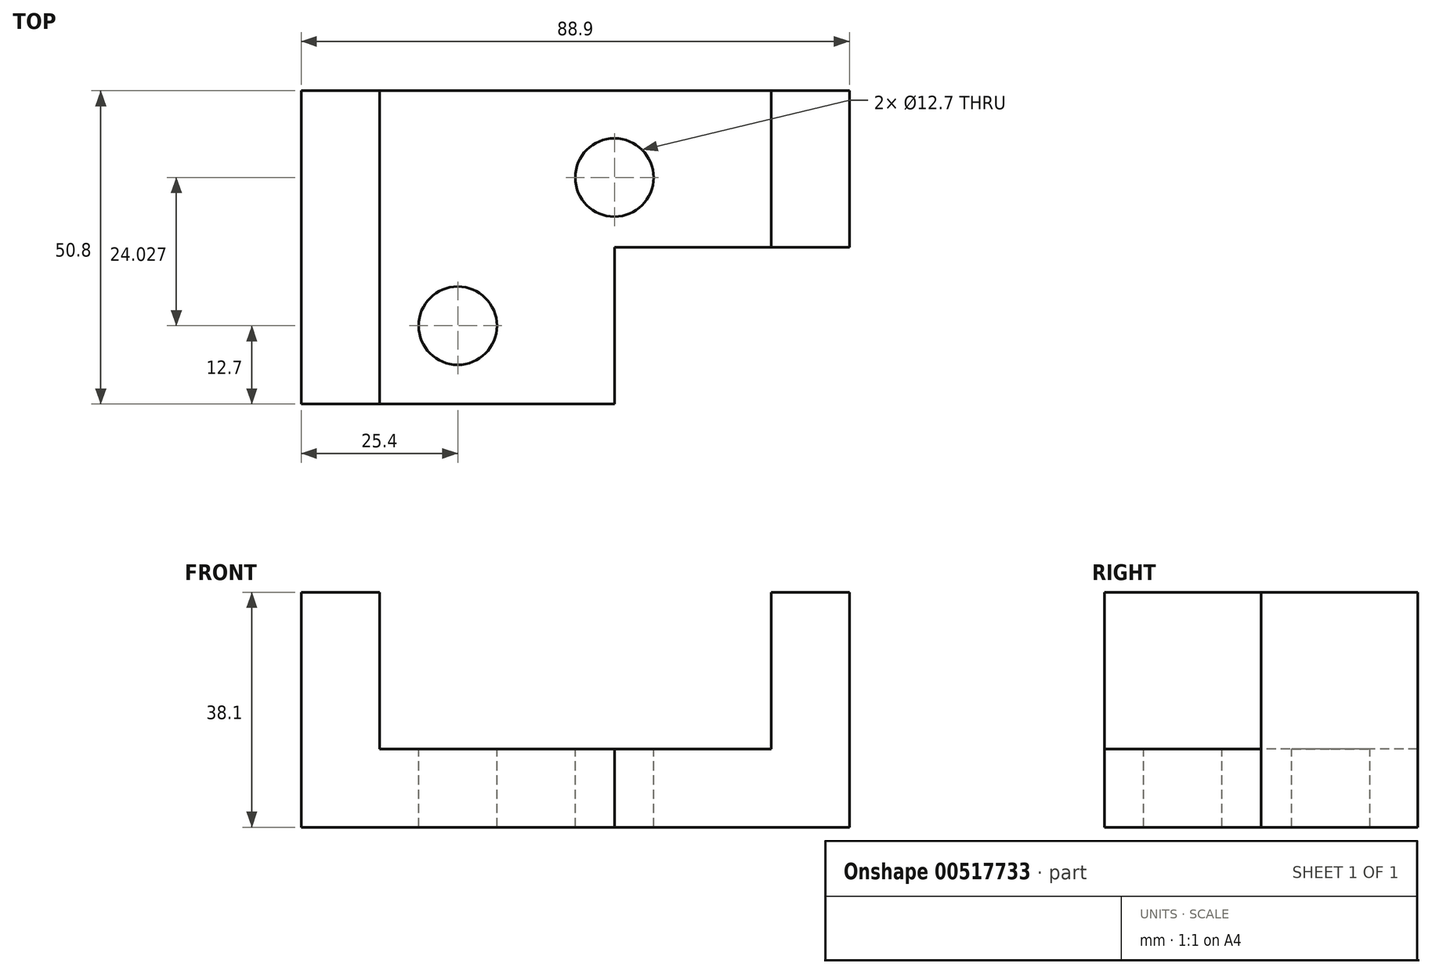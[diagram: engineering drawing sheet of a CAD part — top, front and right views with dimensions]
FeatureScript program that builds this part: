
annotation { "Feature Type Name" : "Feature", "Feature Type Description" : "" }
export const myFeature = defineFeature(function(context is Context, id is Id, definition is map)
    precondition{}
    {
        {
            var Q0;
            Q0=qCreatedBy(makeId("Front.planeOp"),FACE);
            var sketch = newSketch(context, id + "F0", { "sketchPlane" : qUnion([Q0])});
            skLineSegment(sketch, "E0.bottom", {"start": v(-44.45, 19.05) * mm, "end": v(44.45, 19.05) * mm});
            skLineSegment(sketch, "E0.top", {"start": v(-44.45, -19.05) * mm, "end": v(44.45, -19.05) * mm});
            skLineSegment(sketch, "E0.left", {"start": v(-44.45, 19.05) * mm, "end": v(-44.45, -19.05) * mm});
            skLineSegment(sketch, "E0.right", {"start": v(44.45, 19.05) * mm, "end": v(44.45, -19.05) * mm});
            skPoint(sketch, "E0.middle", {"position": v(0, 0) * mm});
            skSolve(sketch);
        }
        {
            var Q0;
            Q0=qSketchRegion(id+"F0",true);
            extrude(context, id + "F1", {"entities" : qUnion([Q0]), "depth" : 50.8 * mm});
        }
        {
            var Q0;
            Q0=makeQuery(id+"F1.opExtrude","CAP_FACE",FACE,{"disambiguationData":[OSD([sQuery(id+"F0.wireOp",EDGE,"E0.bottom"),sQuery(id+"F0.wireOp",EDGE,"E0.top"),sQuery(id+"F0.wireOp",EDGE,"E0.left"),sQuery(id+"F0.wireOp",EDGE,"E0.right")])],"isStart":false});
            var sketch = newSketch(context, id + "F2", { "sketchPlane" : qUnion([Q0])});
            skLineSegment(sketch, "E1.bottom", {"start": v(-31.75, 19.05) * mm, "end": v(31.75, 19.05) * mm});
            skLineSegment(sketch, "E1.top", {"start": v(-31.75, -6.35) * mm, "end": v(31.75, -6.35) * mm});
            skLineSegment(sketch, "E1.left", {"start": v(-31.75, 19.05) * mm, "end": v(-31.75, -6.35) * mm});
            skLineSegment(sketch, "E1.right", {"start": v(31.75, 19.05) * mm, "end": v(31.75, -6.35) * mm});
            skSolve(sketch);
        }
        {
            var Q0;
            Q0=qSketchRegion(id+"F2",true);
            extrude(context, id + "F3", {"entities" : qUnion([Q0]), "operationType" : NewBodyOperationType.REMOVE, "endBound" : BoundingType.THROUGH_ALL, "oppositeDirection" : true, "depth" : 25.4 * mm});
        }
        {
            var Q0;
            {var subQ0=sQuery(id+"F0.wireOp",EDGE,"E0.right");var subQ3=sQuery(id+"F0.wireOp",EDGE,"E0.bottom");Q0=makeQuery(id+"F3.boolean.opBoolean","SPLIT",FACE,{"disambiguationData":[TD([makeQuery(id+"F1.opExtrude","SWEPT_FACE",FACE,{"disambiguationData":[OSD([subQ0])]})])],"derivedFrom":makeQuery(id+"F1.opExtrude","SWEPT_FACE",FACE,{"disambiguationData":[OSD([subQ3])]})});}
            var sketch = newSketch(context, id + "F4", { "sketchPlane" : qUnion([Q0])});
            skLineSegment(sketch, "E2.bottom", {"start": v(44.45, -50.8) * mm, "end": v(6.35, -50.8) * mm});
            skLineSegment(sketch, "E2.top", {"start": v(44.45, -25.4) * mm, "end": v(6.35, -25.4) * mm});
            skLineSegment(sketch, "E2.left", {"start": v(44.45, -50.8) * mm, "end": v(44.45, -25.4) * mm});
            skLineSegment(sketch, "E2.right", {"start": v(6.35, -50.8) * mm, "end": v(6.35, -25.4) * mm});
            skSolve(sketch);
        }
        {
            var Q0;
            Q0=qSketchRegion(id+"F4",true);
            extrude(context, id + "F5", {"entities" : qUnion([Q0]), "operationType" : NewBodyOperationType.REMOVE, "endBound" : BoundingType.THROUGH_ALL, "oppositeDirection" : true, "depth" : 25.4 * mm});
        }
        {
            var Q0;
            Q0=makeQuery(id+"F3.boolean.opBoolean","COPY",FACE,{"derivedFrom":makeQuery(id+"F3.opExtrude","SWEPT_FACE",FACE,{"disambiguationData":[OSD([sQuery(id+"F2.wireOp",EDGE,"E1.top")])]})});
            var sketch = newSketch(context, id + "F6", { "sketchPlane" : qUnion([Q0])});
            skCircle(sketch, "E3", {"center": v(-19.05, -38.1) * mm, "radius": 6.35 * mm});
            skSolve(sketch);
        }
        {
            var Q0;
            Q0=qSketchRegion(id+"F6",true);
            extrude(context, id + "F7", {"entities" : qUnion([Q0]), "operationType" : NewBodyOperationType.REMOVE, "endBound" : BoundingType.THROUGH_ALL, "oppositeDirection" : true, "depth" : 25.4 * mm});
        }
        {
            var Q0;
            Q0=makeQuery(id+"F3.boolean.opBoolean","COPY",FACE,{"derivedFrom":makeQuery(id+"F3.opExtrude","SWEPT_FACE",FACE,{"disambiguationData":[OSD([sQuery(id+"F2.wireOp",EDGE,"E1.top")])]})});
            var sketch = newSketch(context, id + "F8", { "sketchPlane" : qUnion([Q0])});
            skCircle(sketch, "E4", {"center": v(6.35, -14.07) * mm, "radius": 6.35 * mm});
            skSolve(sketch);
        }
        {
            var Q0;
            Q0=qSketchRegion(id+"F8",true);
            extrude(context, id + "F9", {"entities" : qUnion([Q0]), "operationType" : NewBodyOperationType.REMOVE, "endBound" : BoundingType.THROUGH_ALL, "oppositeDirection" : true, "depth" : 25.4 * mm});
        }
    });
